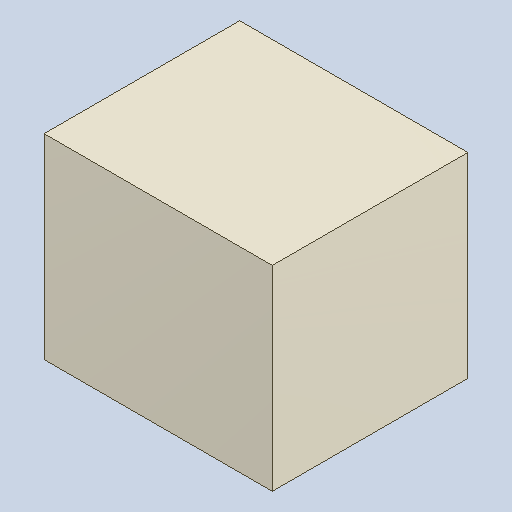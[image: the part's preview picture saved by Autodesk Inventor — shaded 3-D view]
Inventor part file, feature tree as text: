
AUTODESK INVENTOR PART (.ipt)
format: ipt  version: 2023.4 (Build 274418000, 418)  size: 82,432 bytes
history: native  units: mm
features: extrude x1
ambient origin geometry x8: Origin, YZ Plane, XZ Plane, XY Plane, X Axis, Y Axis, Z Axis, Center Point
bodies: Solid1 (feature_tree)
feature tree (1):
  extrude  "Extruded_5"  [1 undecoded]
note: 1 required parameter value undecoded (feature->parameter linkage not recoverable at this tier; creation-order binding heuristic only, values carry confidence <= 0.55)
